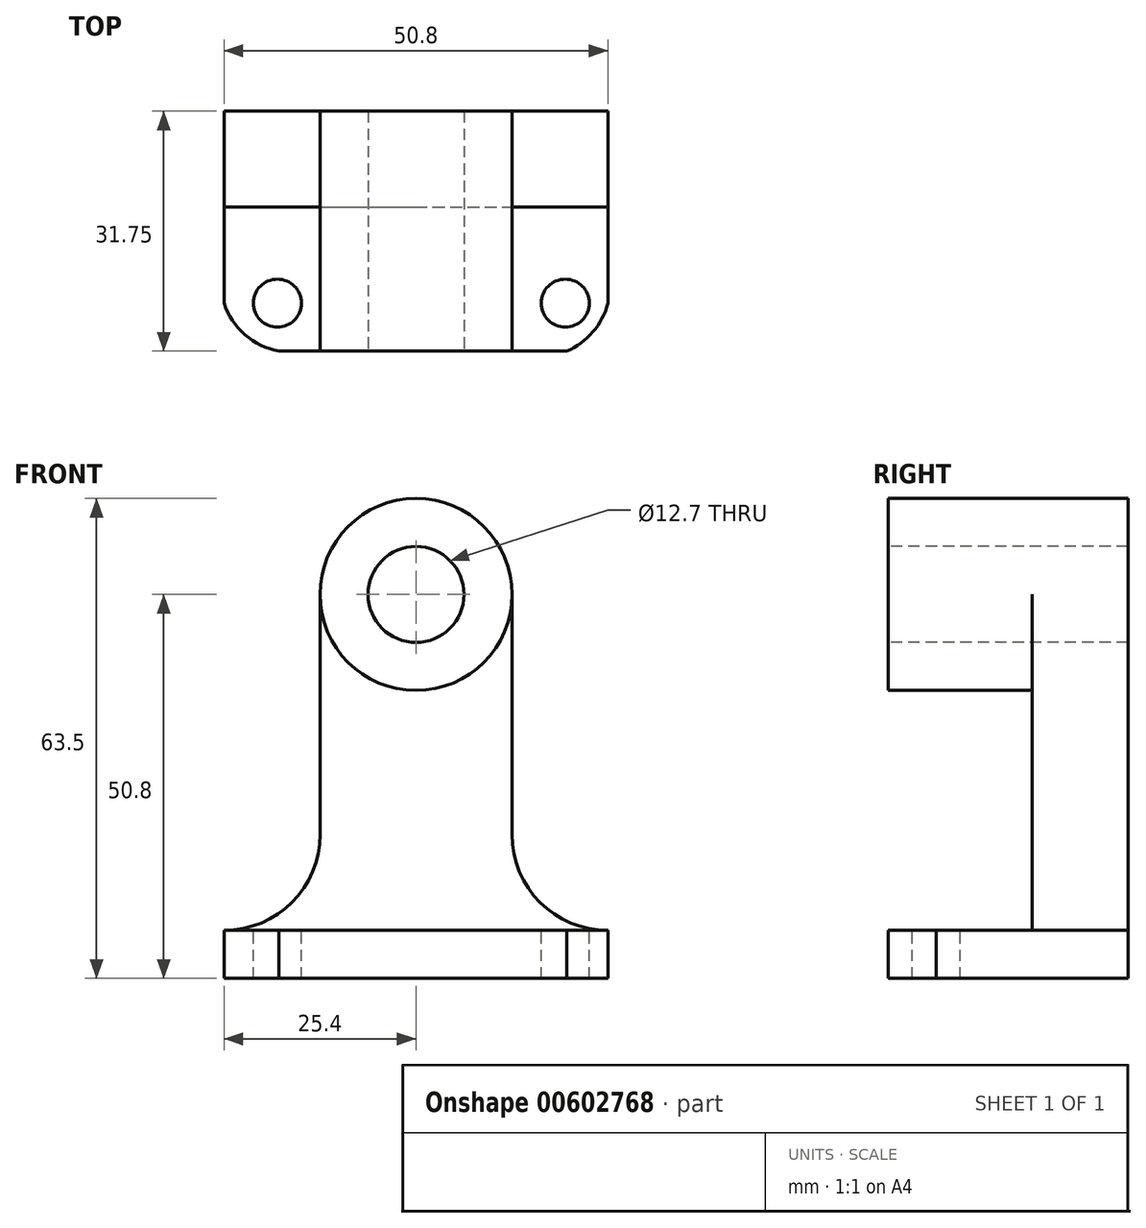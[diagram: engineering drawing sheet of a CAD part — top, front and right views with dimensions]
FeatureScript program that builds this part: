
annotation { "Feature Type Name" : "Feature", "Feature Type Description" : "" }
export const myFeature = defineFeature(function(context is Context, id is Id, definition is map)
    precondition{}
    {
        {
            var Q0;
            Q0=qCreatedBy(makeId("Front.planeOp"),FACE);
            var sketch = newSketch(context, id + "F0", { "sketchPlane" : qUnion([Q0])});
            skLineSegment(sketch, "E0", {"start": v(0, 0) * mm, "end": v(50.8, 0) * mm});
            skLineSegment(sketch, "E1", {"start": v(50.8, 0) * mm, "end": v(50.8, 6.35) * mm});
            skLineSegment(sketch, "E2", {"start": v(50.8, 6.35) * mm, "end": v(50.8, 6.35) * mm});
            skLineSegment(sketch, "E3", {"start": v(50.8, 6.35) * mm, "end": v(50.8, 63.5) * mm});
            skLineSegment(sketch, "E4", {"start": v(50.8, 63.5) * mm, "end": v(0, 63.5) * mm});
            skLineSegment(sketch, "E5", {"start": v(0, 63.5) * mm, "end": v(0, 6.35) * mm});
            skLineSegment(sketch, "E6", {"start": v(0, 6.35) * mm, "end": v(0, 6.35) * mm});
            skLineSegment(sketch, "E7", {"start": v(0, 6.35) * mm, "end": v(0, 0) * mm});
            skSolve(sketch);
        }
        {
            var Q0;
            Q0 = qSketchRegion(id + "F0", true);
            extrude(context, id + "F1", {"entities" : qUnion([Q0]), "depth" : 31.75 * mm, "offsetDistance" : 25.4 * mm});
        }
        {
            var Q0;
            Q0=makeQuery(id+"F1.opExtrude","SWEPT_FACE",FACE,{"disambiguationData":[OSD([sQuery(id+"F0.wireOp",EDGE,"E1"),sQuery(id+"F0.wireOp",EDGE,"E3")])]});
            var sketch = newSketch(context, id + "F2", { "sketchPlane" : qUnion([Q0])});
            skLineSegment(sketch, "E8", {"start": v(-31.75, 6.35) * mm, "end": v(-12.7, 6.35) * mm});
            skLineSegment(sketch, "E9", {"start": v(-12.7, 6.35) * mm, "end": v(-12.7, 38.1) * mm});
            skLineSegment(sketch, "E10", {"start": v(-12.7, 38.1) * mm, "end": v(-31.75, 38.1) * mm});
            skSolve(sketch);
        }
        {
            var Q0;
            {var subQ0=sQuery(id+"F2.wireOp",EDGE,"E8");Q0=makeQuery(id+"F2.imprint","IMPRINT",FACE,{"disambiguationData":[TD([[makeQuery(id+"F2.imprint","IMPRINT",EDGE,{"derivedFrom":subQ0}),1.0]])]});}
            extrude(context, id + "F3", {"entities" : qUnion([Q0]), "operationType" : NewBodyOperationType.REMOVE, "oppositeDirection" : true, "depth" : 57.15 * mm, "offsetDistance" : 25.4 * mm});
        }
        {
            var Q0;
            {var subQ0=sQuery(id+"F0.wireOp",EDGE,"E3");var subQ1=sQuery(id+"F0.wireOp",EDGE,"E1");var subQ2=sQuery(id+"F0.wireOp",EDGE,"E4");var subQ3=sQuery(id+"F0.wireOp",EDGE,"E7");var subQ4=sQuery(id+"F0.wireOp",EDGE,"E5");Q0=makeQuery(id+"F3.boolean.opBoolean","SPLIT",FACE,{"disambiguationData":[TD([makeQuery(id+"F1.opExtrude","SWEPT_FACE",FACE,{"disambiguationData":[OSD([subQ2])]})])],"derivedFrom":makeQuery(id+"F1.opExtrude","CAP_FACE",FACE,{"disambiguationData":[OSD([sQuery(id+"F0.wireOp",EDGE,"E0"),subQ1,subQ0,subQ2,subQ4,subQ3])],"isStart":false})});}
            var sketch = newSketch(context, id + "F4", { "sketchPlane" : qUnion([Q0])});
            skCircle(sketch, "E11", {"center": v(25.4, 50.8) * mm, "radius": 12.7 * mm});
            skSolve(sketch);
        }
        {
            var Q0;
            {var subQ0=sQuery(id+"F4.wireOp",EDGE,"E11");var subQ1=sQuery(id+"F0.wireOp",EDGE,"E4");var subQ2=makeQuery(id+"F1.opExtrude","CAP_EDGE",EDGE,{"disambiguationData":[OSD([subQ1])],"isStart":false});var subQ3=makeQuery(id+"F4.imprint","INTERSECT",VERTEX,{"derivedFrom":[subQ2,subQ0]});Q0=makeQuery(id+"F4.imprint","IMPRINT",FACE,{"disambiguationData":[TD([[makeQuery(id+"F4.imprint","IMPRINT",EDGE,{"disambiguationData":[TD([[subQ3,1.0]])],"derivedFrom":subQ0}),-1.0]])]});}
            var Q1;
            {var subQ0=sQuery(id+"F4.wireOp",EDGE,"E11");var subQ1=sQuery(id+"F0.wireOp",EDGE,"E4");var subQ2=makeQuery(id+"F1.opExtrude","CAP_EDGE",EDGE,{"disambiguationData":[OSD([subQ1])],"isStart":false});var subQ3=makeQuery(id+"F4.imprint","INTERSECT",VERTEX,{"derivedFrom":[subQ2,subQ0]});Q1=makeQuery(id+"F4.imprint","IMPRINT",FACE,{"disambiguationData":[TD([[makeQuery(id+"F4.imprint","IMPRINT",EDGE,{"disambiguationData":[TD([[subQ3,-1.0]])],"derivedFrom":subQ0}),-1.0]])]});}
            extrude(context, id + "F5", {"entities" : qUnion([Q0, Q1]), "operationType" : NewBodyOperationType.REMOVE, "oppositeDirection" : true, "depth" : 19.05 * mm, "offsetDistance" : 25.4 * mm});
        }
        {
            var Q0;
            {var subQ0=sQuery(id+"F4.wireOp",EDGE,"E11");var subQ1=sQuery(id+"F2.wireOp",EDGE,"E10");var subQ2=sQuery(id+"F0.wireOp",EDGE,"E4");var subQ3=sQuery(id+"F0.wireOp",EDGE,"E3");var subQ4=sQuery(id+"F0.wireOp",EDGE,"E1");Q0=makeQuery(id+"F5.boolean.opBoolean","MERGE",FACE,{"derivedFrom":[makeQuery(id+"F3.boolean.opBoolean","COPY",FACE,{"derivedFrom":makeQuery(id+"F3.opExtrude","SWEPT_FACE",FACE,{"disambiguationData":[OSD([sQuery(id+"F2.wireOp",EDGE,"E9")])]})})],"fromTools":[makeQuery(id+"F5.opExtrude","CAP_FACE",FACE,{"disambiguationData":[OSD([subQ4,subQ3,subQ2,sQuery(id+"F0.wireOp",EDGE,"E5"),sQuery(id+"F0.wireOp",EDGE,"E7"),subQ1,subQ0])],"isStart":false}),makeQuery(id+"F5.opExtrude","CAP_FACE",FACE,{"disambiguationData":[OSD([subQ4,subQ3,subQ2,subQ1,subQ0])],"isStart":false})]});}
            var sketch = newSketch(context, id + "F6", { "sketchPlane" : qUnion([Q0])});
            skLineSegment(sketch, "E12.0.0", {"start": v(0, 6.35) * mm, "end": v(50.8, 6.35) * mm});
            skLineSegment(sketch, "E12.0.1", {"start": v(50.8, 6.35) * mm, "end": v(50.8, 63.5) * mm});
            skLineSegment(sketch, "E12.0.2", {"start": v(50.8, 63.5) * mm, "end": v(25.4, 63.5) * mm});
            skCircle(sketch, "E12.0.3", {"center": v(25.4, 50.8) * mm, "radius": 12.7 * mm});
            skLineSegment(sketch, "E12.0.4", {"start": v(25.4, 63.5) * mm, "end": v(0, 63.5) * mm});
            skLineSegment(sketch, "E12.0.5", {"start": v(0, 63.5) * mm, "end": v(0, 6.35) * mm});
            skLineSegment(sketch, "E13", {"start": v(12.7, 50.8) * mm, "end": v(12.7, 19.05) * mm});
            skLineSegment(sketch, "E14", {"start": v(38.1, 50.8) * mm, "end": v(38.1, 19.05) * mm});
            skArc(sketch, "E15", {"start": v(0, 6.35) * mm, "mid": v(8.98, 10.07) * mm, "end": v(12.7, 19.05) * mm});
            skArc(sketch, "E16", {"start": v(38.1, 19.05) * mm, "mid": v(41.82, 10.07) * mm, "end": v(50.8, 6.35) * mm});
            skSolve(sketch);
        }
        {
            var Q0;
            {var subQ1=sQuery(id+"F6.wireOp",EDGE,"E12.0.4");Q0=makeQuery(id+"F6.imprint","IMPRINT",FACE,{"disambiguationData":[TD([[makeQuery(id+"F6.imprint","IMPRINT",EDGE,{"derivedFrom":subQ1}),1.0]])]});}
            var Q1;
            Q1=makeQuery(id+"F6.imprint","IMPRINT",FACE,{"disambiguationData":[TD([[makeQuery(id+"F6.imprint","IMPRINT",EDGE,{"derivedFrom":sQuery(id+"F6.wireOp",EDGE,"E12.0.1")}),1.0]])]});
            extrude(context, id + "F7", {"entities" : qUnion([Q0, Q1]), "operationType" : NewBodyOperationType.REMOVE, "oppositeDirection" : true, "depth" : 25.4 * mm, "offsetDistance" : 25.4 * mm});
        }
        {
            var Q0;
            {var subQ0=sQuery(id+"F0.wireOp",EDGE,"E3");var subQ1=sQuery(id+"F0.wireOp",EDGE,"E1");var subQ2=sQuery(id+"F0.wireOp",EDGE,"E4");var subQ3=sQuery(id+"F0.wireOp",EDGE,"E7");var subQ4=sQuery(id+"F0.wireOp",EDGE,"E5");Q0=makeQuery(id+"F3.boolean.opBoolean","SPLIT",FACE,{"disambiguationData":[TD([makeQuery(id+"F1.opExtrude","SWEPT_FACE",FACE,{"disambiguationData":[OSD([subQ2])]})])],"derivedFrom":makeQuery(id+"F1.opExtrude","CAP_FACE",FACE,{"disambiguationData":[OSD([sQuery(id+"F0.wireOp",EDGE,"E0"),subQ1,subQ0,subQ2,subQ4,subQ3])],"isStart":false})});}
            var sketch = newSketch(context, id + "F8", { "sketchPlane" : qUnion([Q0])});
            skCircle(sketch, "E17", {"center": v(25.4, 50.8) * mm, "radius": 6.35 * mm});
            skSolve(sketch);
        }
        {
            var Q0;
            Q0=makeQuery(id+"F8.imprint","IMPRINT",FACE,{"disambiguationData":[TD([[makeQuery(id+"F8.imprint","IMPRINT",EDGE,{"derivedFrom":sQuery(id+"F8.wireOp",EDGE,"E17")}),1.0]])]});
            extrude(context, id + "F9", {"entities" : qUnion([Q0]), "operationType" : NewBodyOperationType.REMOVE, "oppositeDirection" : true, "depth" : 31.75 * mm, "offsetDistance" : 25.4 * mm});
        }
        {
            var Q0;
            Q0=makeQuery(id+"F3.boolean.opBoolean","COPY",FACE,{"derivedFrom":makeQuery(id+"F3.opExtrude","SWEPT_FACE",FACE,{"disambiguationData":[OSD([sQuery(id+"F2.wireOp",EDGE,"E8")])]})});
            var sketch = newSketch(context, id + "F10", { "sketchPlane" : qUnion([Q0])});
            skLineSegment(sketch, "E18.0.0", {"start": v(0, -31.75) * mm, "end": v(50.8, -31.75) * mm});
            skLineSegment(sketch, "E18.0.1", {"start": v(50.8, -31.75) * mm, "end": v(50.8, -12.7) * mm});
            skLineSegment(sketch, "E18.0.2", {"start": v(50.8, -12.7) * mm, "end": v(0, -12.7) * mm});
            skLineSegment(sketch, "E18.0.3", {"start": v(0, -12.7) * mm, "end": v(0, -31.75) * mm});
            skArc(sketch, "E19", {"start": v(0, -25.4) * mm, "mid": v(2.77, -29.56) * mm, "end": v(7.26, -31.75) * mm});
            skArc(sketch, "E20", {"start": v(45.36, -31.75) * mm, "mid": v(48.81, -29.2) * mm, "end": v(50.8, -25.4) * mm});
            skSolve(sketch);
        }
        {
            var Q0;
            {var subQ3=sQuery(id+"F10.wireOp",EDGE,"E19");Q0=makeQuery(id+"F10.imprint","IMPRINT",FACE,{"disambiguationData":[TD([[makeQuery(id+"F10.imprint","IMPRINT",EDGE,{"derivedFrom":subQ3}),-1.0]])]});}
            var Q1;
            {var subQ3=sQuery(id+"F10.wireOp",EDGE,"E20");Q1=makeQuery(id+"F10.imprint","IMPRINT",FACE,{"disambiguationData":[TD([[makeQuery(id+"F10.imprint","IMPRINT",EDGE,{"derivedFrom":subQ3}),-1.0]])]});}
            extrude(context, id + "F11", {"entities" : qUnion([Q0, Q1]), "operationType" : NewBodyOperationType.REMOVE, "oppositeDirection" : true, "depth" : 6.35 * mm, "offsetDistance" : 25.4 * mm});
        }
        {
            var Q0;
            Q0=makeQuery(id+"F3.boolean.opBoolean","COPY",FACE,{"derivedFrom":makeQuery(id+"F3.opExtrude","SWEPT_FACE",FACE,{"disambiguationData":[OSD([sQuery(id+"F2.wireOp",EDGE,"E8")])]})});
            var sketch = newSketch(context, id + "F12", { "sketchPlane" : qUnion([Q0])});
            skCircle(sketch, "E21", {"center": v(7.06, -25.4) * mm, "radius": 3.18 * mm});
            skCircle(sketch, "E22", {"center": v(45.16, -25.4) * mm, "radius": 3.18 * mm});
            skSolve(sketch);
        }
        {
            var Q0;
            Q0=makeQuery(id+"F12.imprint","IMPRINT",FACE,{"disambiguationData":[TD([[makeQuery(id+"F12.imprint","IMPRINT",EDGE,{"derivedFrom":sQuery(id+"F12.wireOp",EDGE,"E21")}),1.0]])]});
            var Q1;
            Q1=makeQuery(id+"F12.imprint","IMPRINT",FACE,{"disambiguationData":[TD([[makeQuery(id+"F12.imprint","IMPRINT",EDGE,{"derivedFrom":sQuery(id+"F12.wireOp",EDGE,"E22")}),1.0]])]});
            extrude(context, id + "F13", {"entities" : qUnion([Q0, Q1]), "operationType" : NewBodyOperationType.REMOVE, "oppositeDirection" : true, "depth" : 6.35 * mm, "offsetDistance" : 25.4 * mm});
        }
        {
            var Q0;
            Q0 = qSketchRegion(id + "F12", true);
            extrude(context, id + "F14", {"entities" : qUnion([Q0]), "operationType" : NewBodyOperationType.REMOVE, "oppositeDirection" : true, "depth" : 6.35 * mm, "offsetDistance" : 25.4 * mm});
        }
    });
